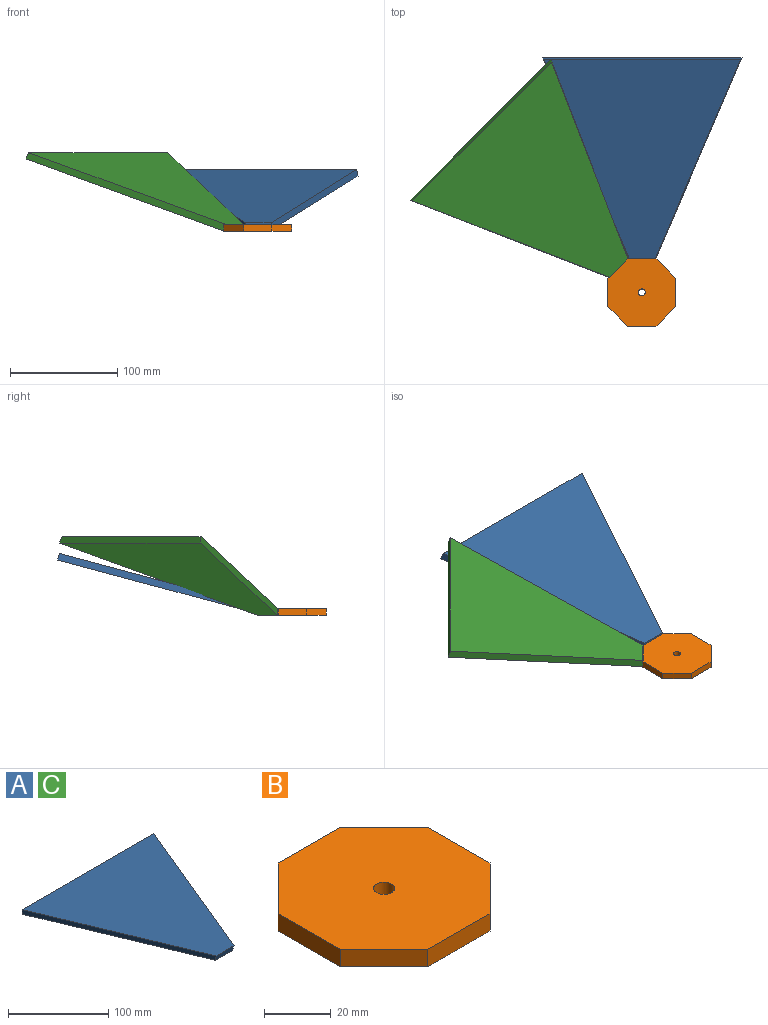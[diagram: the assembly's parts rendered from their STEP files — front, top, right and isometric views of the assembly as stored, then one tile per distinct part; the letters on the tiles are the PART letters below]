
ASSEMBLY  parts=3 mates=1
PART A: 6 faces, bbox 185.8x193.6x6.4 mm
  f0: plane 185.78x6.35mm, normal (0,1,0), area 1171mm2, adj f1,f3,f4,f5
  f1: plane 193.6x80.85mm, normal (-0.91,-0.38,-0.2), area 1350.7mm2, adj f0,f2,f4,f5
  f2: plane 25.4x6.35mm, normal (0,-0.97,-0.26), area 162.6mm2, adj f1,f3,f4,f5
  f3: plane 193.6x80.85mm, normal (0.91,-0.38,-0.2), area 1350.7mm2, adj f0,f2,f4,f5
  f4: plane 193.6x185.78mm, normal (0,0,1), area 20442.4mm2, adj f0,f1,f2,f3
  f5: plane 191.9x183.05mm, normal (0,0,-1), area 19873.2mm2, adj f0,f1,f2,f3
PART B: 11 faces, bbox 63.5x63.5x6.4 mm
  f0: plane 18.6x18.6mm, normal (-0.71,-0.71,0), area 167mm2, adj f1,f7,f8,f9
  f1: plane 26.3x6.35mm, normal (0,-1,0), area 167mm2, adj f0,f2,f8,f9
  f2: plane 18.6x18.6mm, normal (0.71,-0.71,0), area 167mm2, adj f1,f3,f8,f9
  f3: plane 26.3x6.35mm, normal (1,0,0), area 167mm2, adj f2,f4,f8,f9
  f4: plane 18.6x18.6mm, normal (0.71,0.71,0), area 167mm2, adj f3,f5,f8,f9
  f5: plane 26.3x6.35mm, normal (0,1,0), area 167mm2, adj f4,f6,f8,f9
  f6: plane 18.6x18.6mm, normal (-0.71,0.71,0), area 167mm2, adj f5,f7,f8,f9
  f7: plane 26.3x6.35mm, normal (-1,0,0), area 167mm2, adj f0,f6,f8,f9
  f8: plane 63.5x63.5mm, normal (0,0,1), area 3308.8mm2, adj f0,f1,f2,f3,f4,f5,f6,f7
  f9: plane 63.5x63.5mm, normal (0,0,-1), area 3308.8mm2, adj f0,f1,f2,f3,f4,f5,f6,f7
  f10: cylinder r=3.17mm len=6.35mm, axis (0,0,1), area 126.7mm2, adj f8,f9
PART C: same geometry as A
PLACE A rot(axis=(0,-0.99,-0.13),180deg) t=(10.72,53.33,28.83)mm
PLACE B t=(-2.43,23.23,21.26)mm
PLACE C rot(axis=(0.38,-0.91,-0.16),172.2deg) t=(-13.92,53.68,27.24)mm
MATE planar B.f5 <-> A.f2  axis (0,1,0) through (-2.43,54.98,24.44)mm
